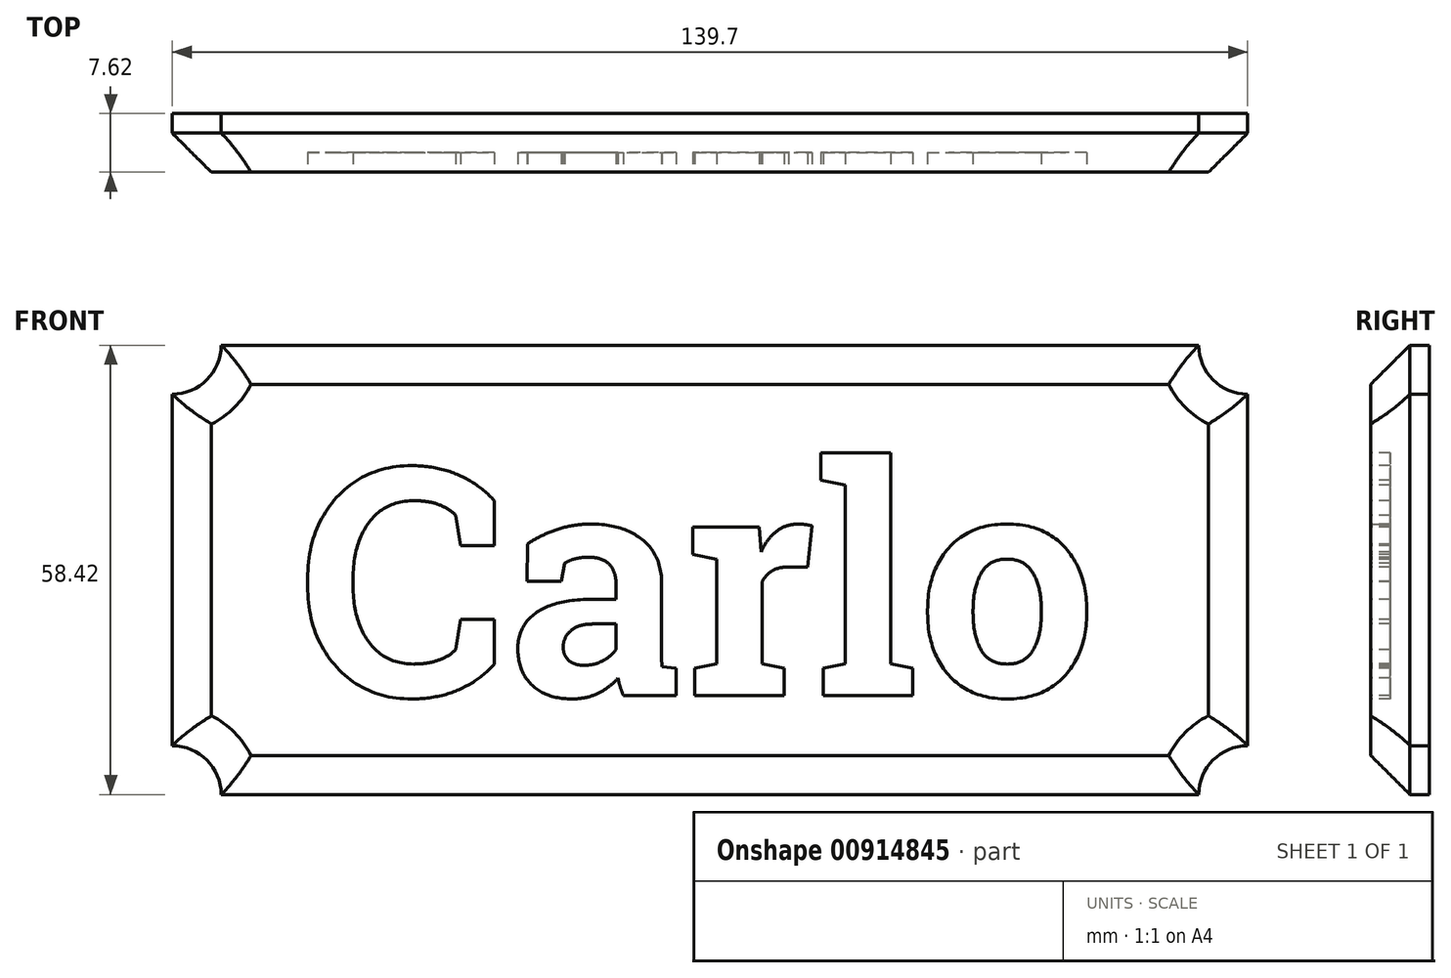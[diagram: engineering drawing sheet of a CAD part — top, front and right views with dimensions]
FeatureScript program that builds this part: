
annotation { "Feature Type Name" : "Feature", "Feature Type Description" : "" }
export const myFeature = defineFeature(function(context is Context, id is Id, definition is map)
    precondition{}
    {
        {
            var Q0;
            Q0=qCreatedBy(makeId("Front.planeOp"),FACE);
            var sketch = newSketch(context, id + "F0", { "sketchPlane" : qUnion([Q0])});
            skLineSegment(sketch, "E0", {"start": v(-67.63, 58.42) * mm, "end": v(72.07, 58.42) * mm});
            skLineSegment(sketch, "E1", {"start": v(-67.63, 58.42) * mm, "end": v(-67.63, 0) * mm});
            skLineSegment(sketch, "E2", {"start": v(-67.63, 0) * mm, "end": v(72.07, 0) * mm});
            skLineSegment(sketch, "E3", {"start": v(72.07, 0) * mm, "end": v(72.07, 58.42) * mm});
            skCircle(sketch, "E4", {"center": v(-67.63, 58.42) * mm, "radius": 6.35 * mm});
            skCircle(sketch, "E5", {"center": v(72.07, 58.42) * mm, "radius": 6.35 * mm});
            skCircle(sketch, "E6", {"center": v(72.07, 0) * mm, "radius": 6.35 * mm});
            skCircle(sketch, "E7", {"center": v(-67.63, 0) * mm, "radius": 6.35 * mm});
            skSolve(sketch);
        }
        {
            var Q0;
            {var subQ11=sQuery(id+"F0.wireOp",EDGE,"E4");var subQ13=sQuery(id+"F0.wireOp",EDGE,"E0");var subQ14=makeQuery(id+"F0.imprint","INTERSECT",VERTEX,{"derivedFrom":[subQ13,subQ11]});Q0=makeQuery(id+"F0.imprint","IMPRINT",FACE,{"disambiguationData":[TD([[makeQuery(id+"F0.imprint","IMPRINT",EDGE,{"disambiguationData":[TD([[subQ14,-1.0]])],"derivedFrom":subQ13}),-1.0]])]});}
            extrude(context, id + "F1", {"entities" : qUnion([Q0]), "depth" : 7.62 * mm, "offsetDistance" : 25.4 * mm});
        }
        {
            var Q0;
            Q0=makeQuery(id+"F1.opExtrude","CAP_EDGE",EDGE,{"disambiguationData":[OSD([sQuery(id+"F0.wireOp",EDGE,"E0")])],"isStart":false});
            var Q1;
            Q1=makeQuery(id+"F1.opExtrude","CAP_EDGE",EDGE,{"disambiguationData":[OSD([sQuery(id+"F0.wireOp",EDGE,"E1")])],"isStart":false});
            var Q2;
            Q2=makeQuery(id+"F1.opExtrude","CAP_EDGE",EDGE,{"disambiguationData":[OSD([sQuery(id+"F0.wireOp",EDGE,"E2")])],"isStart":false});
            var Q3;
            Q3=makeQuery(id+"F1.opExtrude","CAP_EDGE",EDGE,{"disambiguationData":[OSD([sQuery(id+"F0.wireOp",EDGE,"E3")])],"isStart":false});
            var Q4;
            Q4=makeQuery(id+"F1.opExtrude","CAP_EDGE",EDGE,{"disambiguationData":[OSD([sQuery(id+"F0.wireOp",EDGE,"E6")])],"isStart":false});
            var Q5;
            Q5=makeQuery(id+"F1.opExtrude","CAP_EDGE",EDGE,{"disambiguationData":[OSD([sQuery(id+"F0.wireOp",EDGE,"E5")])],"isStart":false});
            var Q6;
            Q6=makeQuery(id+"F1.opExtrude","CAP_EDGE",EDGE,{"disambiguationData":[OSD([sQuery(id+"F0.wireOp",EDGE,"E4")])],"isStart":false});
            var Q7;
            Q7=makeQuery(id+"F1.opExtrude","CAP_EDGE",EDGE,{"disambiguationData":[OSD([sQuery(id+"F0.wireOp",EDGE,"E7")])],"isStart":false});
            chamfer(context, id + "F2", {"entities" : qUnion([Q0, Q1, Q2, Q3, Q4, Q5, Q6, Q7]), "width" : 5.08 * mm, "tangentPropagation" : true});
        }
        {
            var Q0;
            Q0=makeQuery(id+"F1.opExtrude","CAP_FACE",FACE,{"disambiguationData":[OSD([sQuery(id+"F0.wireOp",EDGE,"E0"),sQuery(id+"F0.wireOp",EDGE,"E1"),sQuery(id+"F0.wireOp",EDGE,"E2"),sQuery(id+"F0.wireOp",EDGE,"E3"),sQuery(id+"F0.wireOp",EDGE,"E4"),sQuery(id+"F0.wireOp",EDGE,"E5"),sQuery(id+"F0.wireOp",EDGE,"E6"),sQuery(id+"F0.wireOp",EDGE,"E7")])],"isStart":false});
            var sketch = newSketch(context, id + "F3", { "sketchPlane" : qUnion([Q0])});
            skText(sketch, "E8", { "text": "Carlo", "fontName": "RobotoSlab-Bold.ttf"});
            const initialGuessF3  = {"E8": [-0.0511, 0.01286, 1, 0, 0.02985]};
            skSetInitialGuess(sketch, initialGuessF3);
            skSolve(sketch);
        }
        {
            var Q0;
            Q0 = qSketchRegion(id + "F3", true);
            extrude(context, id + "F4", {"entities" : qUnion([Q0]), "operationType" : NewBodyOperationType.REMOVE, "oppositeDirection" : true, "depth" : 2.54 * mm, "offsetDistance" : 25.4 * mm});
        }
    });
